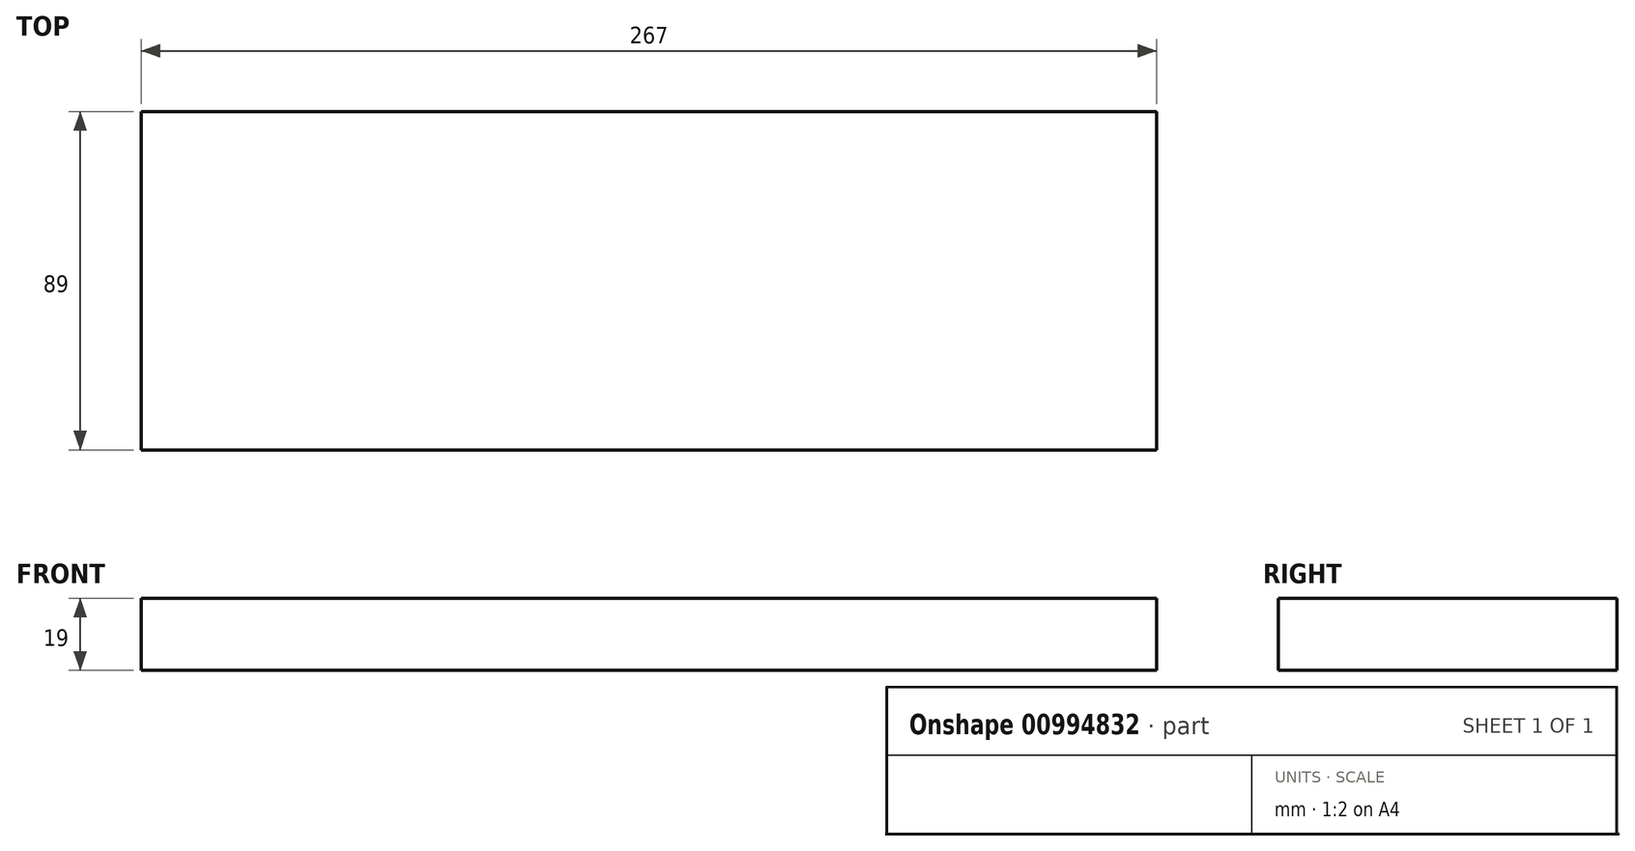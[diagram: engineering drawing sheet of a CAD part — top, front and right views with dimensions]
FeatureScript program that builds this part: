
annotation { "Feature Type Name" : "Feature", "Feature Type Description" : "" }
export const myFeature = defineFeature(function(context is Context, id is Id, definition is map)
    precondition{}
    {
        {
            var Q0;
            Q0=qCreatedBy(makeId("Top.planeOp"),FACE);
            var sketch = newSketch(context, id + "F0", { "sketchPlane" : qUnion([Q0])});
            skLineSegment(sketch, "E0.bottom", {"start": v(0, 89) * mm, "end": v(267, 89) * mm});
            skLineSegment(sketch, "E0.top", {"start": v(0, 0) * mm, "end": v(267, 0) * mm});
            skLineSegment(sketch, "E0.left", {"start": v(0, 89) * mm, "end": v(0, 0) * mm});
            skLineSegment(sketch, "E0.right", {"start": v(267, 89) * mm, "end": v(267, 0) * mm});
            skSolve(sketch);
        }
        {
            var Q0;
            Q0=qSketchRegion(id+"F0",true);
            extrude(context, id + "F1", {"entities" : qUnion([Q0]), "depth" : 19 * mm});
        }
    });
